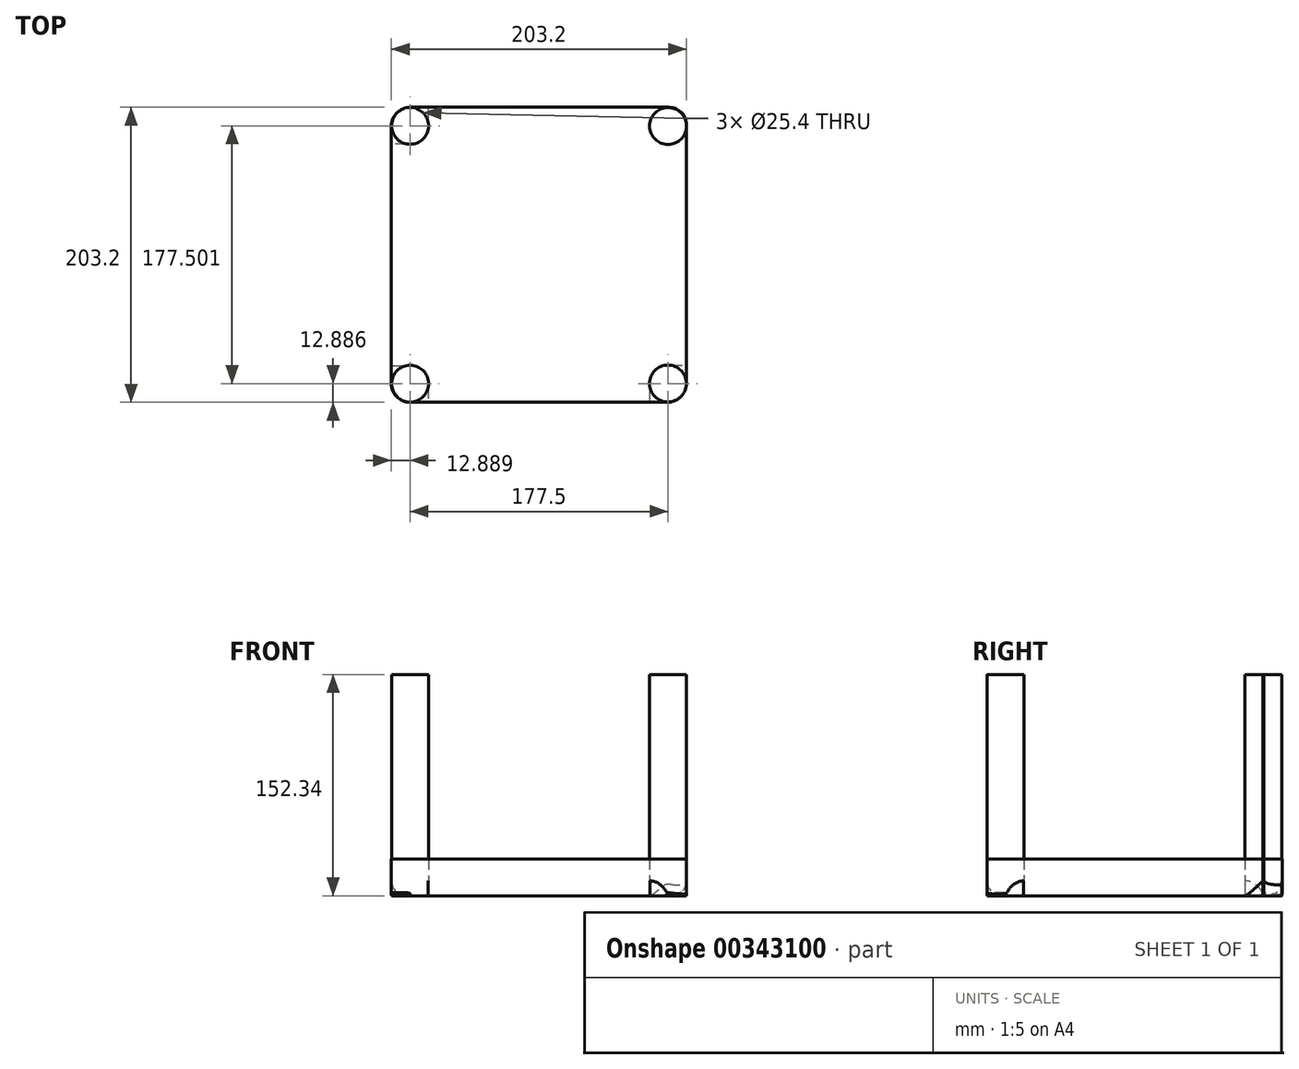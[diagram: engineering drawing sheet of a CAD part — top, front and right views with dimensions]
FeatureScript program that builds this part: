
annotation { "Feature Type Name" : "Feature", "Feature Type Description" : "" }
export const myFeature = defineFeature(function(context is Context, id is Id, definition is map)
    precondition{}
    {
        {
            var Q0;
            Q0=qCreatedBy(makeId("Top.planeOp"),FACE);
            var sketch = newSketch(context, id + "F0", { "sketchPlane" : qUnion([Q0])});
            skLineSegment(sketch, "E0.bottom", {"start": v(101.6, 101.6) * mm, "end": v(-101.6, 101.6) * mm});
            skLineSegment(sketch, "E0.top", {"start": v(101.6, -101.6) * mm, "end": v(-101.6, -101.6) * mm});
            skLineSegment(sketch, "E0.left", {"start": v(101.6, 101.6) * mm, "end": v(101.6, -101.6) * mm});
            skLineSegment(sketch, "E0.right", {"start": v(-101.6, 101.6) * mm, "end": v(-101.6, -101.6) * mm});
            skPoint(sketch, "E0.middle", {"position": v(0, 0) * mm});
            skCircle(sketch, "E1", {"center": v(-88.71, -88.71) * mm, "radius": 12.7 * mm});
            skCircle(sketch, "E2", {"center": v(88.79, -88.68) * mm, "radius": 12.7 * mm});
            skCircle(sketch, "E3", {"center": v(-88.7, 88.79) * mm, "radius": 12.7 * mm});
            skCircle(sketch, "E4", {"center": v(88.9, 88.7) * mm, "radius": 12.7 * mm});
            skSolve(sketch);
        }
        {
            var Q0;
            {var subQ0=sQuery(id+"F0.wireOp",EDGE,"E4");var subQ1=sQuery(id+"F0.wireOp",EDGE,"E0.left");var subQ2=makeQuery(id+"F0.imprint","INTERSECT",VERTEX,{"disambiguationData":[OD(0.0)],"derivedFrom":[subQ1,subQ0]});Q0=makeQuery(id+"F0.imprint","IMPRINT",FACE,{"disambiguationData":[TD([[makeQuery(id+"F0.imprint","IMPRINT",EDGE,{"disambiguationData":[TD([[subQ2,-1.0]])],"derivedFrom":subQ1}),-1.0]])]});}
            var Q1;
            Q1=makeQuery(id+"F0.imprint","IMPRINT",FACE,{"disambiguationData":[TD([[makeQuery(id+"F0.imprint","IMPRINT",EDGE,{"derivedFrom":sQuery(id+"F0.wireOp",EDGE,"E1")}),1.0]])]});
            var Q2;
            Q2=makeQuery(id+"F0.imprint","IMPRINT",FACE,{"disambiguationData":[TD([[makeQuery(id+"F0.imprint","IMPRINT",EDGE,{"derivedFrom":sQuery(id+"F0.wireOp",EDGE,"E3")}),1.0]])]});
            var Q3;
            Q3=makeQuery(id+"F0.imprint","IMPRINT",FACE,{"disambiguationData":[TD([[makeQuery(id+"F0.imprint","IMPRINT",EDGE,{"derivedFrom":sQuery(id+"F0.wireOp",EDGE,"E2")}),1.0]])]});
            extrude(context, id + "F1", {"entities" : qUnion([Q0, Q1, Q2, Q3]), "depth" : 152.34 * mm});
        }
        {
            var Q0;
            {var subQ4=sQuery(id+"F0.wireOp",EDGE,"E0.bottom");Q0=makeQuery(id+"F0.imprint","IMPRINT",FACE,{"disambiguationData":[TD([[makeQuery(id+"F0.imprint","IMPRINT",EDGE,{"derivedFrom":subQ4}),1.0]])]});}
            extrude(context, id + "F2", {"entities" : qUnion([Q0]), "depth" : 25.4 * mm});
        }
        {
            var Q0;
            Q0=makeQuery(id+"F2.opExtrude","SWEPT_EDGE",EDGE,{"disambiguationData":[OSD([sQuery(id+"F0.wireOp",EDGE,"E0.bottom"),sQuery(id+"F0.wireOp",EDGE,"E0.left")])]});
            fillet(context, id + "F3", {"entities" : qUnion([Q0]), "radius" : 12.07 * mm, "tangentPropagation" : true, "allowEdgeOverflow" : false});
        }
        {
            var Q0;
            Q0=makeQuery(id+"F2.opExtrude","SWEPT_EDGE",EDGE,{"disambiguationData":[OSD([sQuery(id+"F0.wireOp",EDGE,"E0.bottom"),sQuery(id+"F0.wireOp",EDGE,"E0.right")])]});
            fillet(context, id + "F4", {"entities" : qUnion([Q0]), "radius" : 13.18 * mm, "tangentPropagation" : true, "allowEdgeOverflow" : false});
        }
        {
            var Q0;
            Q0=makeQuery(id+"F2.opExtrude","SWEPT_EDGE",EDGE,{"disambiguationData":[OSD([sQuery(id+"F0.wireOp",EDGE,"E0.top"),sQuery(id+"F0.wireOp",EDGE,"E0.right")])]});
            fillet(context, id + "F5", {"entities" : qUnion([Q0]), "radius" : 12.85 * mm, "tangentPropagation" : true, "allowEdgeOverflow" : false});
        }
        {
            var Q0;
            Q0=makeQuery(id+"F2.opExtrude","SWEPT_EDGE",EDGE,{"disambiguationData":[OSD([sQuery(id+"F0.wireOp",EDGE,"E0.top"),sQuery(id+"F0.wireOp",EDGE,"E0.left")])]});
            fillet(context, id + "F6", {"entities" : qUnion([Q0]), "radius" : 13.08 * mm, "tangentPropagation" : true, "allowEdgeOverflow" : false});
        }
        {
            var Q0;
            Q0=makeQuery(id+"F2.opExtrude","CAP_EDGE",EDGE,{"disambiguationData":[OSD([sQuery(id+"F0.wireOp",EDGE,"E0.bottom")])],"isStart":true});
            fillet(context, id + "F7", {"entities" : qUnion([Q0]), "radius" : 10.3 * mm, "tangentPropagation" : true, "allowEdgeOverflow" : false});
        }
    });
